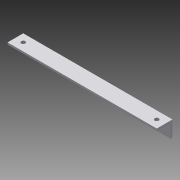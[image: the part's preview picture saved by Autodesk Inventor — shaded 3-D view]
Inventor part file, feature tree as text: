
AUTODESK INVENTOR PART (.ipt)
format: ipt  version: 2015 (Build 190159000, 159)  size: 101,888 bytes
history: native  units: in
note: dims shown in document units (in); Inventor stores cm internally (conversion verified against a paired STEP export)
features: sketch x2, extrude x1, hole x1, projected_geometry x1
ambient origin geometry x8: Origin, YZ Plane, XZ Plane, XY Plane, X Axis, Y Axis, Z Axis, Center Point
bodies: Solid1 (feature_tree)
feature tree (5):
  extrude  "Extrusion1"  Depth=1.0in
  hole  "Hole1"  [1 undecoded]
  sketch  "Sketch1"  dims[d0=0.125in d1=1.0in]
  sketch  "Sketch2"  dims[d2=1.0in d3=0.125in d4=9.5in d5=0.0in d6=0.5in d7=0.5in d8=0.5in d9=9.0in d10=0.2656in d11=0.75in d12=0.375in d13=0.25in d14=0.5635in d15=1.0in d16=0.8108in]
  projected_geometry  "Projected Loop1"
note: 1 required parameter value undecoded (feature->parameter linkage not recoverable at this tier; creation-order binding heuristic only, values carry confidence <= 0.55)
